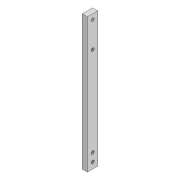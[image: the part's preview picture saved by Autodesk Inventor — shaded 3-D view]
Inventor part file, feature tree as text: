
AUTODESK INVENTOR PART (.ipt)
format: ipt  version: 2022 (Build 260153000, 153)  size: 94,208 bytes
history: native  units: mm
features: extrude x1
ambient origin geometry x8: Origin, YZ Plane, XZ Plane, XY Plane, X Axis, Y Axis, Z Axis, Center Point
bodies: Solid1 (feature_tree)
feature tree (1):
  extrude  "Extrusion1"  Depth=130.0mm
